# Revit family: З-ВО
name_source: partatom
category: Арматура воздуховодов
units: mm (PartAtom-declared; Revit-internal decimal feet)

## family parameters
Всегда вертикально = Да
На основе рабочей плоскости = Нет
Общий = Нет
При загрузке вырезать с полостями = Нет
Размер круглого соединителя = Использовать диаметр
Тип детали = Присоединяется

## types (11) — shared parameters
00_20_Manufacturer = Вентс
00_20_Name = Зонт
Casing Material = Условный материал-отделка
Grid Material = Условный материал-отделка
Load Classification = HVAC
Maintenance zone material = <По категории>
zero-valued in all types: Отметка по умолчанию

## per-type parameters (varying)
| type | A | A1 | D2 | Dn | Dy | H | a | a1 | h | h1 | Вес |
| З-ВО-400 | 612 мм | 490 мм | 490 мм | 405 мм | 400 мм | 319 мм | 353 мм | 283 мм | 150 мм | 85 мм | 10 кг |
| З-ВО-450 | 672 мм | 538 мм | 540 мм | 455 мм | 450 мм | 319 мм | 388 мм | 310 мм | 150 мм | 85 мм | 11 кг |
| З-ВО-1250 | 1707 мм | 1366 мм | 1400 мм | 1255 мм | 1250 мм | 685 мм | 986 мм | 788 мм | 285 мм | 200 мм | 115 кг |
| З-ВО-500 | 742 мм | 594 мм | 600 мм | 505 мм | 500 мм | 350 мм | 428 мм | 343 мм | 150 мм | 100 мм | 14 кг |
| З-ВО-560 | 790 мм | 632 мм | 660 мм | 565 мм | 560 мм | 350 мм | 456 мм | 365 мм | 150 мм | 100 мм | 16 кг |
| З-ВО-630 | 860 мм | 688 мм | 730 мм | 635 мм | 630 мм | 359 мм | 497 мм | 397 мм | 150 мм | 105 мм | 20 кг |
| З-ВО-710 | 988 мм | 790 мм | 810 мм | 715 мм | 710 мм | 420 мм | 570 мм | 456 мм | 150 мм | 135 мм | 31 кг |
| З-ВО-800 | 1072 мм | 858 мм | 900 мм | 805 мм | 800 мм | 475 мм | 619 мм | 495 мм | 190 мм | 143 мм | 42 кг |
| З-ВО-900 | 1189 мм | 951 мм | 1015 мм | 905 мм | 900 мм | 527 мм | 686 мм | 549 мм | 210 мм | 159 мм | 57 кг |
| З-ВО-1000 | 1404 мм | 1123 мм | 1115 мм | 1005 мм | 1000 мм | 640 мм | 811 мм | 648 мм | 240 мм | 200 мм | 83 кг |
| З-ВО-1120 | 1552 мм | 1242 мм | 1270 мм | 1125 мм | 1120 мм | 655 мм | 896 мм | 717 мм | 255 мм | 200 мм | 99 кг |

note: column(s) folded — value = type name in every type: 00_20_Type
